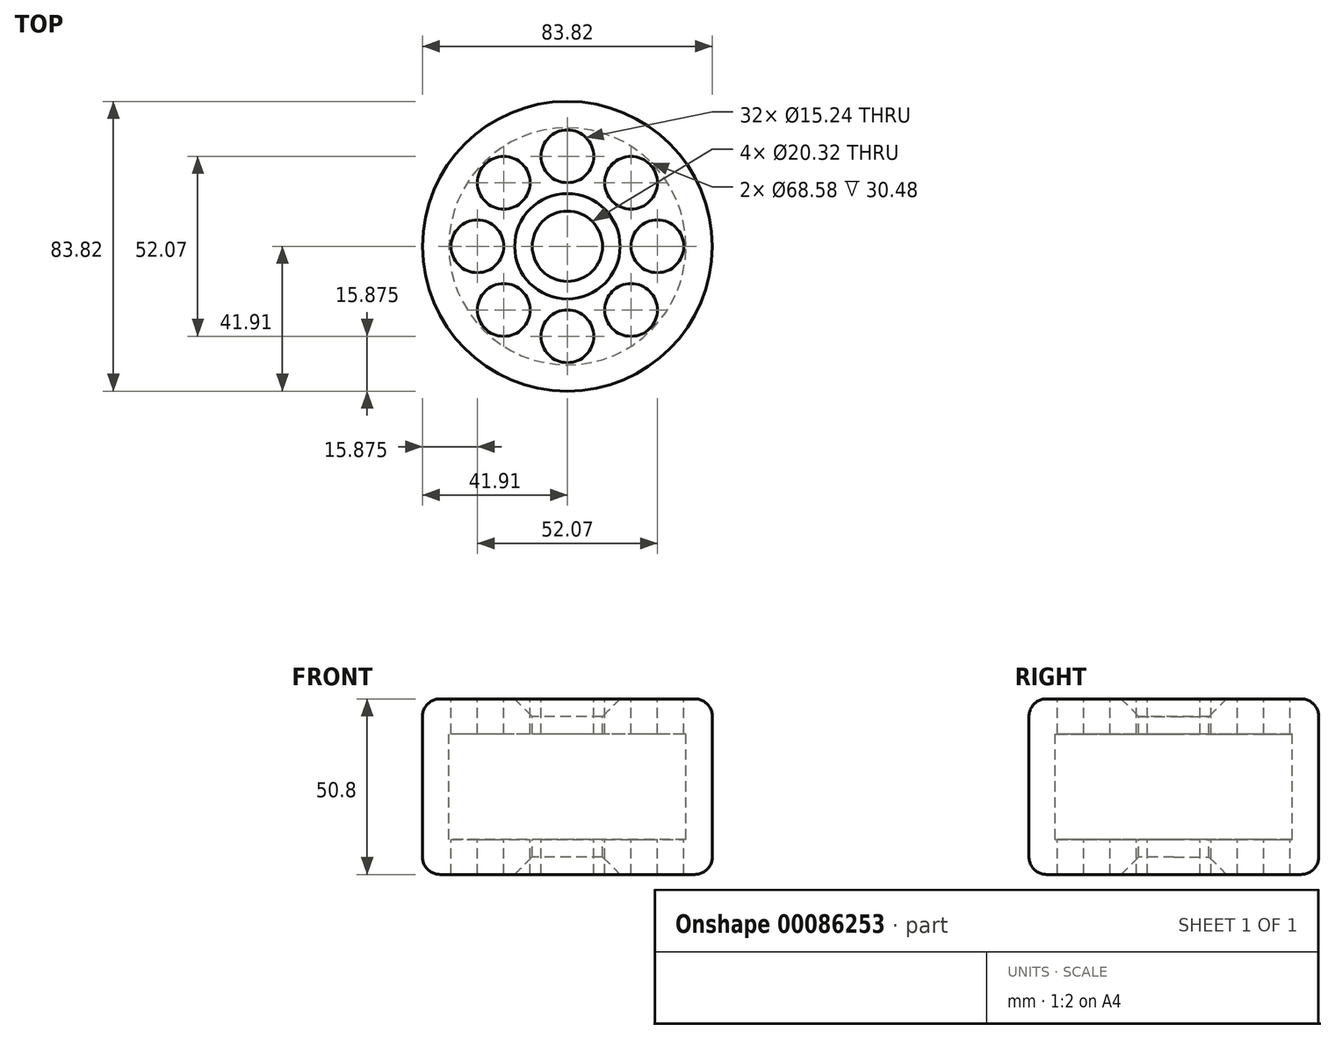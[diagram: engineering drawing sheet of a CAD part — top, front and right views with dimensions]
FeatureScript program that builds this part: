
annotation { "Feature Type Name" : "Feature", "Feature Type Description" : "" }
export const myFeature = defineFeature(function(context is Context, id is Id, definition is map)
    precondition{}
    {
        {
            var Q0;
            Q0=qCreatedBy(makeId("Front.planeOp"),FACE);
            var sketch = newSketch(context, id + "F0", { "sketchPlane" : qUnion([Q0])});
            skLineSegment(sketch, "E0", {"start": v(-10.16, 42.34) * mm, "end": v(-41.91, 42.34) * mm});
            skLineSegment(sketch, "E1", {"start": v(-41.91, 42.34) * mm, "end": v(-41.91, -8.46) * mm});
            skLineSegment(sketch, "E2", {"start": v(-41.9, -8.46) * mm, "end": v(-10.16, -8.46) * mm});
            skLineSegment(sketch, "E3", {"start": v(-10.16, -8.46) * mm, "end": v(-10.16, 1.7) * mm});
            skLineSegment(sketch, "E4", {"start": v(-10.16, 32.18) * mm, "end": v(-34.3, 32.18) * mm});
            skLineSegment(sketch, "E5", {"start": v(-34.3, 32.18) * mm, "end": v(-34.3, 1.7) * mm});
            skLineSegment(sketch, "E6", {"start": v(-34.3, 1.7) * mm, "end": v(-10.16, 1.7) * mm});
            skLineSegment(sketch, "E7.trimOffspring", {"start": v(-10.16, 32.18) * mm, "end": v(-10.16, 42.34) * mm});
            skLineSegment(sketch, "E8", {"start": v(0, 76.39) * mm, "end": v(0, -76.01) * mm, "construction": true});
            skSolve(sketch);
        }
        {
            var Q0;
            Q0=makeQuery(id+"F0.imprint","IMPRINT",FACE,{"disambiguationData":[TD([[makeQuery(id+"F0.imprint","IMPRINT",EDGE,{"derivedFrom":sQuery(id+"F0.wireOp",EDGE,"E0")}),1.0]])]});
            var Q1;
            Q1=sQuery(id+"F0.wireOp",EDGE,"E8");
            revolve(context, id + "F1", {"entities" : qUnion([Q0]), "axis" : qUnion([Q1]), "revolveType" : RevolveType.FULL});
        }
        {
            var Q0;
            Q0=makeQuery(id+"F1.opRevolve","SWEPT_EDGE",EDGE,{"disambiguationData":[OSD([sQuery(id+"F0.wireOp",EDGE,"E0"),sQuery(id+"F0.wireOp",EDGE,"E1")])]});
            var Q1;
            Q1=makeQuery(id+"F1.opRevolve","SWEPT_EDGE",EDGE,{"disambiguationData":[OSD([sQuery(id+"F0.wireOp",EDGE,"E1"),sQuery(id+"F0.wireOp",EDGE,"E2")])]});
            fillet(context, id + "F2", {"entities" : qUnion([Q0, Q1]), "radius" : 5.08 * mm, "tangentPropagation" : true, "allowEdgeOverflow" : false});
        }
        {
            var Q0;
            Q0=makeQuery(id+"F1.opRevolve","SWEPT_EDGE",EDGE,{"disambiguationData":[OSD([sQuery(id+"F0.wireOp",EDGE,"E0"),sQuery(id+"F0.wireOp",EDGE,"E7.trimOffspring")])]});
            var Q1;
            Q1=makeQuery(id+"F1.opRevolve","SWEPT_EDGE",EDGE,{"disambiguationData":[OSD([sQuery(id+"F0.wireOp",EDGE,"E2"),sQuery(id+"F0.wireOp",EDGE,"E3")])]});
            chamfer(context, id + "F3", {"entities" : qUnion([Q0, Q1]), "width" : 5.08 * mm, "tangentPropagation" : true});
        }
        {
            var Q0;
            Q0=makeQuery(id+"F1.opRevolve","SWEPT_FACE",FACE,{"disambiguationData":[OSD([sQuery(id+"F0.wireOp",EDGE,"E0")])]});
            var sketch = newSketch(context, id + "F4", { "sketchPlane" : qUnion([Q0])});
            skCircle(sketch, "E9", {"center": v(0, 26.04) * mm, "radius": 7.62 * mm});
            skCircle(sketch, "E10.1.0", {"center": v(-18.4, 18.4) * mm, "radius": 7.62 * mm});
            skCircle(sketch, "E10.2.0", {"center": v(-26.04, 0) * mm, "radius": 7.62 * mm});
            skCircle(sketch, "E10.3.0", {"center": v(-18.4, -18.4) * mm, "radius": 7.62 * mm});
            skCircle(sketch, "E10.4.0", {"center": v(0, -26.04) * mm, "radius": 7.62 * mm});
            skCircle(sketch, "E10.5.0", {"center": v(18.4, -18.4) * mm, "radius": 7.62 * mm});
            skCircle(sketch, "E10.6.0", {"center": v(26.04, 0) * mm, "radius": 7.62 * mm});
            skCircle(sketch, "E10.7.0", {"center": v(18.4, 18.4) * mm, "radius": 7.62 * mm});
            skPoint(sketch, "E10.center", {"position": v(0, 0) * mm});
            skSolve(sketch);
        }
        {
            var Q0;
            Q0=makeQuery(id+"F4.imprint","IMPRINT",FACE,{"disambiguationData":[TD([[makeQuery(id+"F4.imprint","IMPRINT",EDGE,{"derivedFrom":sQuery(id+"F4.wireOp",EDGE,"E10.3.0")}),1.0]])]});
            var Q1;
            Q1=makeQuery(id+"F4.imprint","IMPRINT",FACE,{"disambiguationData":[TD([[makeQuery(id+"F4.imprint","IMPRINT",EDGE,{"derivedFrom":sQuery(id+"F4.wireOp",EDGE,"E10.4.0")}),1.0]])]});
            var Q2;
            Q2=makeQuery(id+"F4.imprint","IMPRINT",FACE,{"disambiguationData":[TD([[makeQuery(id+"F4.imprint","IMPRINT",EDGE,{"derivedFrom":sQuery(id+"F4.wireOp",EDGE,"E10.5.0")}),1.0]])]});
            var Q3;
            Q3=makeQuery(id+"F4.imprint","IMPRINT",FACE,{"disambiguationData":[TD([[makeQuery(id+"F4.imprint","IMPRINT",EDGE,{"derivedFrom":sQuery(id+"F4.wireOp",EDGE,"E10.6.0")}),1.0]])]});
            var Q4;
            Q4=makeQuery(id+"F4.imprint","IMPRINT",FACE,{"disambiguationData":[TD([[makeQuery(id+"F4.imprint","IMPRINT",EDGE,{"derivedFrom":sQuery(id+"F4.wireOp",EDGE,"E10.7.0")}),1.0]])]});
            var Q5;
            Q5=makeQuery(id+"F4.imprint","IMPRINT",FACE,{"disambiguationData":[TD([[makeQuery(id+"F4.imprint","IMPRINT",EDGE,{"derivedFrom":sQuery(id+"F4.wireOp",EDGE,"E9")}),1.0]])]});
            var Q6;
            Q6=makeQuery(id+"F4.imprint","IMPRINT",FACE,{"disambiguationData":[TD([[makeQuery(id+"F4.imprint","IMPRINT",EDGE,{"derivedFrom":sQuery(id+"F4.wireOp",EDGE,"E10.1.0")}),1.0]])]});
            var Q7;
            Q7=makeQuery(id+"F4.imprint","IMPRINT",FACE,{"disambiguationData":[TD([[makeQuery(id+"F4.imprint","IMPRINT",EDGE,{"derivedFrom":sQuery(id+"F4.wireOp",EDGE,"E10.2.0")}),1.0]])]});
            extrude(context, id + "F5", {"entities" : qUnion([Q0, Q1, Q2, Q3, Q4, Q5, Q6, Q7]), "operationType" : NewBodyOperationType.REMOVE, "endBound" : BoundingType.THROUGH_ALL, "oppositeDirection" : true, "depth" : 25.4 * mm});
        }
        {
            var Q0;
            Q0=makeQuery(id+"F1.opRevolve","SWEPT_BODY",BODY,{"disambiguationData":[OSD([sQuery(id+"F0.wireOp",EDGE,"E0"),sQuery(id+"F0.wireOp",EDGE,"E1"),sQuery(id+"F0.wireOp",EDGE,"E2"),sQuery(id+"F0.wireOp",EDGE,"E3"),sQuery(id+"F0.wireOp",EDGE,"E4"),sQuery(id+"F0.wireOp",EDGE,"E5"),sQuery(id+"F0.wireOp",EDGE,"E6"),sQuery(id+"F0.wireOp",EDGE,"E7.trimOffspring")])]});
            transform(context, id + "F6", {"entities" : qUnion([Q0]), "transformType" : TransformType.TRANSLATION_3D, "dx" : 0 * mm, "dy" : 0 * mm, "dz" : 0 * mm, "makeCopy" : true});
        }
    });
